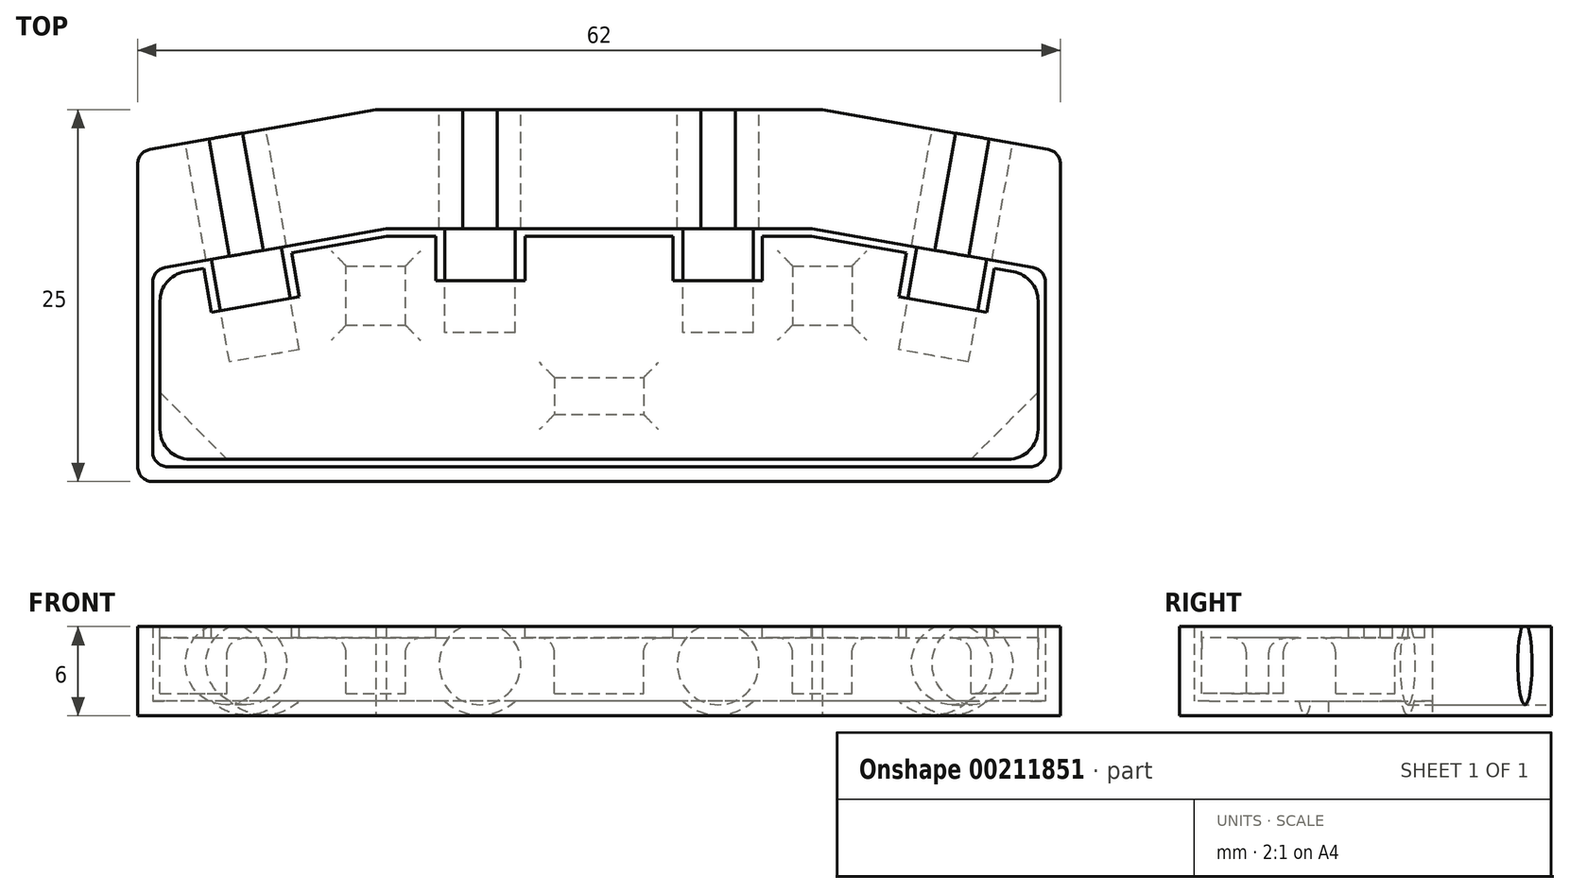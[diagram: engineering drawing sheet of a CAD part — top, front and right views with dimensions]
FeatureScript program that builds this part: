
annotation { "Feature Type Name" : "Feature", "Feature Type Description" : "" }
export const myFeature = defineFeature(function(context is Context, id is Id, definition is map)
    precondition{}
    {
        {
            var Q0;
            Q0=qCreatedBy(makeId("Top.planeOp"),FACE);
            var sketch = newSketch(context, id + "F0", { "sketchPlane" : qUnion([Q0])});
            skLineSegment(sketch, "E0.top", {"start": v(-31, -12.5) * mm, "end": v(31, -12.5) * mm});
            skLineSegment(sketch, "E0.left", {"start": v(-31, 12.5) * mm, "end": v(-31, -12.5) * mm});
            skLineSegment(sketch, "E0.right", {"start": v(31, 12.5) * mm, "end": v(31, -12.5) * mm});
            skLineSegment(sketch, "E1", {"start": v(0, 0) * mm, "end": v(31, 0) * mm, "construction": true});
            skLineSegment(sketch, "E2", {"start": v(0, 0) * mm, "end": v(-31, 0) * mm, "construction": true});
            skLineSegment(sketch, "E3", {"start": v(0, 0) * mm, "end": v(0, -12.5) * mm, "construction": true});
            skLineSegment(sketch, "E4", {"start": v(0, 0) * mm, "end": v(0, 12.5) * mm, "construction": true});
            skLineSegment(sketch, "E5", {"start": v(-15, 12.5) * mm, "end": v(-31, 9.68) * mm});
            skLineSegment(sketch, "E6", {"start": v(15, 12.5) * mm, "end": v(31, 9.68) * mm});
            skLineSegment(sketch, "E7", {"start": v(0, 12.5) * mm, "end": v(15, 12.5) * mm});
            skLineSegment(sketch, "E8", {"start": v(31, 12.5) * mm, "end": v(15, 12.5) * mm});
            skLineSegment(sketch, "E9", {"start": v(-31, 12.5) * mm, "end": v(-15, 12.5) * mm});
            skLineSegment(sketch, "E10", {"start": v(-15, 12.5) * mm, "end": v(0, 12.5) * mm});
            skLineSegment(sketch, "E11", {"start": v(-31, 1.56) * mm, "end": v(-14.3, 4.5) * mm});
            skLineSegment(sketch, "E12", {"start": v(14.3, 4.5) * mm, "end": v(31, 1.56) * mm});
            skLineSegment(sketch, "E13", {"start": v(-14.3, 4.5) * mm, "end": v(0, 4.5) * mm});
            skLineSegment(sketch, "E14", {"start": v(0, 4.5) * mm, "end": v(14.3, 4.5) * mm});
            skLineSegment(sketch, "E15", {"start": v(-30, 1.73) * mm, "end": v(-30, -11.5) * mm});
            skLineSegment(sketch, "E16", {"start": v(-30, -11.5) * mm, "end": v(30, -11.5) * mm});
            skLineSegment(sketch, "E17", {"start": v(30, -11.5) * mm, "end": v(30, 1.73) * mm});
            skLineSegment(sketch, "E18", {"start": v(31, -8.28) * mm, "end": v(30, -8.28) * mm, "construction": true});
            skLineSegment(sketch, "E19", {"start": v(27.47, -11.5) * mm, "end": v(27.47, -12.5) * mm, "construction": true});
            skLineSegment(sketch, "E20", {"start": v(-31, -9.5) * mm, "end": v(-30, -9.5) * mm, "construction": true});
            skSolve(sketch);
        }
        {
            var Q0;
            {var subQ3=sQuery(id+"F0.wireOp",EDGE,"E5");Q0=makeQuery(id+"F0.imprint","IMPRINT",FACE,{"disambiguationData":[TD([[makeQuery(id+"F0.imprint","IMPRINT",EDGE,{"derivedFrom":subQ3}),1.0]])]});}
            var Q1;
            {var subQ1=sQuery(id+"F0.wireOp",EDGE,"E0.top");Q1=makeQuery(id+"F0.imprint","IMPRINT",FACE,{"disambiguationData":[TD([[makeQuery(id+"F0.imprint","IMPRINT",EDGE,{"derivedFrom":subQ1}),1.0]])]});}
            var Q2;
            {var subQ1=sQuery(id+"F0.wireOp",EDGE,"E13");Q2=makeQuery(id+"F0.imprint","IMPRINT",FACE,{"disambiguationData":[TD([[makeQuery(id+"F0.imprint","IMPRINT",EDGE,{"derivedFrom":subQ1}),-1.0]])]});}
            extrude(context, id + "F1", {"entities" : qUnion([Q0, Q1, Q2]), "depth" : 1 * mm});
        }
        {
            var Q0;
            {var subQ8=sQuery(id+"F0.wireOp",EDGE,"E5");Q0=makeQuery(id+"F0.imprint","IMPRINT",FACE,{"disambiguationData":[TD([[makeQuery(id+"F0.imprint","IMPRINT",EDGE,{"derivedFrom":subQ8}),1.0]])]});}
            var Q1;
            {var subQ1=sQuery(id+"F0.wireOp",EDGE,"E0.top");Q1=makeQuery(id+"F0.imprint","IMPRINT",FACE,{"disambiguationData":[TD([[makeQuery(id+"F0.imprint","IMPRINT",EDGE,{"derivedFrom":subQ1}),1.0]])]});}
            extrude(context, id + "F2", {"entities" : qUnion([Q0, Q1]), "operationType" : NewBodyOperationType.ADD, "depth" : 6 * mm});
        }
        {
            var Q0;
            {var subQ0=sQuery(id+"F0.wireOp",EDGE,"E10");var subQ1=sQuery(id+"F0.wireOp",EDGE,"E7");Q0=makeQuery(id+"F2.boolean.opBoolean","MERGE",FACE,{"derivedFrom":[makeQuery(id+"F1.opExtrude","SWEPT_FACE",FACE,{"disambiguationData":[OSD([subQ1,sQuery(id+"F0.wireOp",EDGE,"E8"),sQuery(id+"F0.wireOp",EDGE,"E9"),subQ0])]}),makeQuery(id+"F2.opExtrude","SWEPT_FACE",FACE,{"disambiguationData":[OSD([subQ1,subQ0])]})]});}
            var sketch = newSketch(context, id + "F3", { "sketchPlane" : qUnion([Q0])});
            skCircle(sketch, "E21", {"center": v(-8, 3.5) * mm, "radius": 2.75 * mm});
            skCircle(sketch, "E22", {"center": v(8, 3.5) * mm, "radius": 2.75 * mm});
            skLineSegment(sketch, "E23", {"start": v(-8, 3.5) * mm, "end": v(0, 3.5) * mm, "construction": true});
            skLineSegment(sketch, "E24", {"start": v(0, 3.5) * mm, "end": v(8, 3.5) * mm, "construction": true});
            skLineSegment(sketch, "E25", {"start": v(0, 3.5) * mm, "end": v(0, 6) * mm, "construction": true});
            skLineSegment(sketch, "E26", {"start": v(0, 3.5) * mm, "end": v(0, 0) * mm, "construction": true});
            skCircle(sketch, "E27", {"center": v(-8, 3.5) * mm, "radius": 3.45 * mm});
            skCircle(sketch, "E28", {"center": v(8, 3.5) * mm, "radius": 3.45 * mm});
            skSolve(sketch);
        }
        {
            var Q0;
            {var subQ0=sQuery(id+"F3.wireOp",EDGE,"E21");var subQ1=makeQuery(id+"F2.opExtrude","CAP_EDGE",EDGE,{"disambiguationData":[OSD([sQuery(id+"F0.wireOp",EDGE,"E7"),sQuery(id+"F0.wireOp",EDGE,"E10")])],"isStart":false});var subQ2=makeQuery(id+"F3.imprint","INTERSECT",VERTEX,{"disambiguationData":[OD(0.0)],"derivedFrom":[subQ1,subQ0]});Q0=makeQuery(id+"F3.imprint","IMPRINT",FACE,{"disambiguationData":[TD([[makeQuery(id+"F3.imprint","IMPRINT",EDGE,{"disambiguationData":[TD([[subQ2,-1.0]])],"derivedFrom":subQ0}),1.0]])]});}
            var Q1;
            {var subQ0=sQuery(id+"F3.wireOp",EDGE,"E22");var subQ1=makeQuery(id+"F2.opExtrude","CAP_EDGE",EDGE,{"disambiguationData":[OSD([sQuery(id+"F0.wireOp",EDGE,"E7"),sQuery(id+"F0.wireOp",EDGE,"E10")])],"isStart":false});var subQ2=makeQuery(id+"F3.imprint","INTERSECT",VERTEX,{"disambiguationData":[OD(0.0)],"derivedFrom":[subQ1,subQ0]});Q1=makeQuery(id+"F3.imprint","IMPRINT",FACE,{"disambiguationData":[TD([[makeQuery(id+"F3.imprint","IMPRINT",EDGE,{"disambiguationData":[TD([[subQ2,1.0]])],"derivedFrom":subQ0}),1.0]])]});}
            var Q2;
            {var subQ0=sQuery(id+"F3.wireOp",EDGE,"E22");var subQ1=makeQuery(id+"F2.opExtrude","CAP_EDGE",EDGE,{"disambiguationData":[OSD([sQuery(id+"F0.wireOp",EDGE,"E7"),sQuery(id+"F0.wireOp",EDGE,"E10")])],"isStart":false});var subQ2=makeQuery(id+"F3.imprint","INTERSECT",VERTEX,{"disambiguationData":[OD(0.0)],"derivedFrom":[subQ1,subQ0]});Q2=makeQuery(id+"F3.imprint","IMPRINT",FACE,{"disambiguationData":[TD([[makeQuery(id+"F3.imprint","IMPRINT",EDGE,{"disambiguationData":[TD([[subQ2,-1.0]])],"derivedFrom":subQ0}),1.0]])]});}
            extrude(context, id + "F4", {"entities" : qUnion([Q0, Q1, Q2]), "operationType" : NewBodyOperationType.REMOVE, "oppositeDirection" : true, "depth" : 8 * mm});
        }
        {
            var Q0;
            Q0=makeQuery(id+"F2.opExtrude","SWEPT_FACE",FACE,{"disambiguationData":[OSD([sQuery(id+"F0.wireOp",EDGE,"E6")])]});
            var sketch = newSketch(context, id + "F5", { "sketchPlane" : qUnion([Q0])});
            skCircle(sketch, "E29", {"center": v(-22.85, 3.5) * mm, "radius": 2.75 * mm});
            skCircle(sketch, "E30", {"center": v(-22.85, 3.5) * mm, "radius": 3.45 * mm});
            skSolve(sketch);
        }
        {
            var Q0;
            {var subQ0=sQuery(id+"F5.wireOp",EDGE,"E29");var subQ1=makeQuery(id+"F2.opExtrude","CAP_EDGE",EDGE,{"disambiguationData":[OSD([sQuery(id+"F0.wireOp",EDGE,"E6")])],"isStart":false});var subQ2=makeQuery(id+"F5.imprint","INTERSECT",VERTEX,{"disambiguationData":[OD(0.0)],"derivedFrom":[subQ1,subQ0]});Q0=makeQuery(id+"F5.imprint","IMPRINT",FACE,{"disambiguationData":[TD([[makeQuery(id+"F5.imprint","IMPRINT",EDGE,{"disambiguationData":[TD([[subQ2,-1.0]])],"derivedFrom":subQ0}),1.0]])]});}
            var Q1;
            {var subQ0=sQuery(id+"F5.wireOp",EDGE,"E29");var subQ1=makeQuery(id+"F2.opExtrude","CAP_EDGE",EDGE,{"disambiguationData":[OSD([sQuery(id+"F0.wireOp",EDGE,"E6")])],"isStart":false});var subQ2=makeQuery(id+"F5.imprint","INTERSECT",VERTEX,{"disambiguationData":[OD(0.0)],"derivedFrom":[subQ1,subQ0]});Q1=makeQuery(id+"F5.imprint","IMPRINT",FACE,{"disambiguationData":[TD([[makeQuery(id+"F5.imprint","IMPRINT",EDGE,{"disambiguationData":[TD([[subQ2,1.0]])],"derivedFrom":subQ0}),1.0]])]});}
            extrude(context, id + "F6", {"entities" : qUnion([Q0, Q1]), "operationType" : NewBodyOperationType.REMOVE, "oppositeDirection" : true, "depth" : 8 * mm});
        }
        {
            var Q0;
            {var subQ0=sQuery(id+"F0.wireOp",EDGE,"E5");Q0=makeQuery(id+"F2.boolean.opBoolean","MERGE",FACE,{"derivedFrom":[makeQuery(id+"F1.opExtrude","SWEPT_FACE",FACE,{"disambiguationData":[OSD([subQ0])]}),makeQuery(id+"F2.opExtrude","SWEPT_FACE",FACE,{"disambiguationData":[OSD([subQ0])]})]});}
            var sketch = newSketch(context, id + "F7", { "sketchPlane" : qUnion([Q0])});
            skCircle(sketch, "E31", {"center": v(22.85, 3.5) * mm, "radius": 2.75 * mm});
            skCircle(sketch, "E32", {"center": v(22.85, 3.5) * mm, "radius": 3.45 * mm});
            skSolve(sketch);
        }
        {
            var Q0;
            {var subQ0=sQuery(id+"F7.wireOp",EDGE,"E31");var subQ1=makeQuery(id+"F2.opExtrude","CAP_EDGE",EDGE,{"disambiguationData":[OSD([sQuery(id+"F0.wireOp",EDGE,"E5")])],"isStart":false});var subQ2=makeQuery(id+"F7.imprint","INTERSECT",VERTEX,{"disambiguationData":[OD(0.0)],"derivedFrom":[subQ1,subQ0]});Q0=makeQuery(id+"F7.imprint","IMPRINT",FACE,{"disambiguationData":[TD([[makeQuery(id+"F7.imprint","IMPRINT",EDGE,{"disambiguationData":[TD([[subQ2,-1.0]])],"derivedFrom":subQ0}),1.0]])]});}
            extrude(context, id + "F8", {"entities" : qUnion([Q0]), "operationType" : NewBodyOperationType.REMOVE, "oppositeDirection" : true, "depth" : 8 * mm});
        }
        {
            var Q0;
            {var subQ0=sQuery(id+"F5.wireOp",EDGE,"E29");var subQ1=makeQuery(id+"F2.opExtrude","CAP_EDGE",EDGE,{"disambiguationData":[OSD([sQuery(id+"F0.wireOp",EDGE,"E6")])],"isStart":false});var subQ2=makeQuery(id+"F5.imprint","INTERSECT",VERTEX,{"disambiguationData":[OD(0.0)],"derivedFrom":[subQ1,subQ0]});Q0=makeQuery(id+"F5.imprint","IMPRINT",FACE,{"disambiguationData":[TD([[makeQuery(id+"F5.imprint","IMPRINT",EDGE,{"disambiguationData":[TD([[subQ2,-1.0]])],"derivedFrom":subQ0}),1.0]])]});}
            var Q1;
            {var subQ1=sQuery(id+"F0.wireOp",EDGE,"E6");var subQ2=makeQuery(id+"F2.opExtrude","CAP_EDGE",EDGE,{"disambiguationData":[OSD([subQ1])],"isStart":false});var subQ6=sQuery(id+"F5.wireOp",EDGE,"E29");var subQ7=makeQuery(id+"F5.imprint","INTERSECT",VERTEX,{"disambiguationData":[OD(0.0)],"derivedFrom":[subQ2,subQ6]});Q1=makeQuery(id+"F5.imprint","IMPRINT",FACE,{"disambiguationData":[TD([[makeQuery(id+"F5.imprint","IMPRINT",EDGE,{"disambiguationData":[TD([[subQ7,-1.0]])],"derivedFrom":subQ6}),-1.0]])]});}
            extrude(context, id + "F9", {"entities" : qUnion([Q0, Q1]), "depth" : -15 * mm, "hasSecondDirection" : true, "secondDirectionOppositeDirection" : false, "secondDirectionDepth" : -8 * mm});
        }
        {
            var Q0;
            {var subQ1=sQuery(id+"F0.wireOp",EDGE,"E10");var subQ2=sQuery(id+"F0.wireOp",EDGE,"E7");var subQ3=makeQuery(id+"F2.opExtrude","CAP_EDGE",EDGE,{"disambiguationData":[OSD([subQ2,subQ1])],"isStart":false});var subQ5=sQuery(id+"F3.wireOp",EDGE,"E21");var subQ6=makeQuery(id+"F3.imprint","INTERSECT",VERTEX,{"disambiguationData":[OD(0.0)],"derivedFrom":[subQ3,subQ5]});Q0=makeQuery(id+"F3.imprint","IMPRINT",FACE,{"disambiguationData":[TD([[makeQuery(id+"F3.imprint","IMPRINT",EDGE,{"disambiguationData":[TD([[subQ6,-1.0]])],"derivedFrom":subQ5}),-1.0]])]});}
            var Q1;
            {var subQ0=sQuery(id+"F3.wireOp",EDGE,"E21");var subQ1=makeQuery(id+"F2.opExtrude","CAP_EDGE",EDGE,{"disambiguationData":[OSD([sQuery(id+"F0.wireOp",EDGE,"E7"),sQuery(id+"F0.wireOp",EDGE,"E10")])],"isStart":false});var subQ2=makeQuery(id+"F3.imprint","INTERSECT",VERTEX,{"disambiguationData":[OD(0.0)],"derivedFrom":[subQ1,subQ0]});Q1=makeQuery(id+"F3.imprint","IMPRINT",FACE,{"disambiguationData":[TD([[makeQuery(id+"F3.imprint","IMPRINT",EDGE,{"disambiguationData":[TD([[subQ2,-1.0]])],"derivedFrom":subQ0}),1.0]])]});}
            var Q2;
            {var subQ1=sQuery(id+"F0.wireOp",EDGE,"E10");var subQ2=sQuery(id+"F0.wireOp",EDGE,"E7");var subQ3=makeQuery(id+"F2.opExtrude","CAP_EDGE",EDGE,{"disambiguationData":[OSD([subQ2,subQ1])],"isStart":false});var subQ5=sQuery(id+"F3.wireOp",EDGE,"E22");var subQ6=makeQuery(id+"F3.imprint","INTERSECT",VERTEX,{"disambiguationData":[OD(0.0)],"derivedFrom":[subQ3,subQ5]});Q2=makeQuery(id+"F3.imprint","IMPRINT",FACE,{"disambiguationData":[TD([[makeQuery(id+"F3.imprint","IMPRINT",EDGE,{"disambiguationData":[TD([[subQ6,-1.0]])],"derivedFrom":subQ5}),-1.0]])]});}
            var Q3;
            {var subQ0=sQuery(id+"F3.wireOp",EDGE,"E22");var subQ1=makeQuery(id+"F2.opExtrude","CAP_EDGE",EDGE,{"disambiguationData":[OSD([sQuery(id+"F0.wireOp",EDGE,"E7"),sQuery(id+"F0.wireOp",EDGE,"E10")])],"isStart":false});var subQ2=makeQuery(id+"F3.imprint","INTERSECT",VERTEX,{"disambiguationData":[OD(0.0)],"derivedFrom":[subQ1,subQ0]});Q3=makeQuery(id+"F3.imprint","IMPRINT",FACE,{"disambiguationData":[TD([[makeQuery(id+"F3.imprint","IMPRINT",EDGE,{"disambiguationData":[TD([[subQ2,-1.0]])],"derivedFrom":subQ0}),1.0]])]});}
            extrude(context, id + "F10", {"entities" : qUnion([Q0, Q1, Q2, Q3]), "oppositeDirection" : true, "depth" : 15 * mm, "hasSecondDirection" : true, "secondDirectionOppositeDirection" : true, "secondDirectionDepth" : 8 * mm});
        }
        {
            var Q0;
            {var subQ1=sQuery(id+"F0.wireOp",EDGE,"E5");var subQ2=makeQuery(id+"F2.opExtrude","CAP_EDGE",EDGE,{"disambiguationData":[OSD([subQ1])],"isStart":false});var subQ6=sQuery(id+"F7.wireOp",EDGE,"E31");var subQ7=makeQuery(id+"F7.imprint","INTERSECT",VERTEX,{"disambiguationData":[OD(0.0)],"derivedFrom":[subQ2,subQ6]});Q0=makeQuery(id+"F7.imprint","IMPRINT",FACE,{"disambiguationData":[TD([[makeQuery(id+"F7.imprint","IMPRINT",EDGE,{"disambiguationData":[TD([[subQ7,-1.0]])],"derivedFrom":subQ6}),-1.0]])]});}
            var Q1;
            {var subQ0=sQuery(id+"F7.wireOp",EDGE,"E31");var subQ1=makeQuery(id+"F2.opExtrude","CAP_EDGE",EDGE,{"disambiguationData":[OSD([sQuery(id+"F0.wireOp",EDGE,"E5")])],"isStart":false});var subQ2=makeQuery(id+"F7.imprint","INTERSECT",VERTEX,{"disambiguationData":[OD(0.0)],"derivedFrom":[subQ1,subQ0]});Q1=makeQuery(id+"F7.imprint","IMPRINT",FACE,{"disambiguationData":[TD([[makeQuery(id+"F7.imprint","IMPRINT",EDGE,{"disambiguationData":[TD([[subQ2,-1.0]])],"derivedFrom":subQ0}),1.0]])]});}
            extrude(context, id + "F11", {"entities" : qUnion([Q0, Q1]), "oppositeDirection" : true, "depth" : 15 * mm, "hasSecondDirection" : true, "secondDirectionOppositeDirection" : true, "secondDirectionDepth" : 8 * mm});
        }
        {
            var Q0;
            {var subQ0=sQuery(id+"F5.wireOp",EDGE,"E29");var subQ1=makeQuery(id+"F2.opExtrude","CAP_EDGE",EDGE,{"disambiguationData":[OSD([sQuery(id+"F0.wireOp",EDGE,"E6")])],"isStart":false});var subQ2=makeQuery(id+"F5.imprint","INTERSECT",VERTEX,{"disambiguationData":[OD(0.0)],"derivedFrom":[subQ1,subQ0]});Q0=makeQuery(id+"F5.imprint","IMPRINT",FACE,{"disambiguationData":[TD([[makeQuery(id+"F5.imprint","IMPRINT",EDGE,{"disambiguationData":[TD([[subQ2,1.0]])],"derivedFrom":subQ0}),-1.0]])]});}
            var Q1;
            {var subQ0=sQuery(id+"F5.wireOp",EDGE,"E29");var subQ1=makeQuery(id+"F2.opExtrude","CAP_EDGE",EDGE,{"disambiguationData":[OSD([sQuery(id+"F0.wireOp",EDGE,"E6")])],"isStart":false});var subQ2=makeQuery(id+"F5.imprint","INTERSECT",VERTEX,{"disambiguationData":[OD(0.0)],"derivedFrom":[subQ1,subQ0]});Q1=makeQuery(id+"F5.imprint","IMPRINT",FACE,{"disambiguationData":[TD([[makeQuery(id+"F5.imprint","IMPRINT",EDGE,{"disambiguationData":[TD([[subQ2,1.0]])],"derivedFrom":subQ0}),1.0]])]});}
            extrude(context, id + "F12", {"entities" : qUnion([Q0, Q1]), "operationType" : NewBodyOperationType.REMOVE, "oppositeDirection" : true, "depth" : 15 * mm, "hasSecondDirection" : true, "secondDirectionOppositeDirection" : true, "secondDirectionDepth" : 8 * mm});
        }
        {
            var Q0;
            Q0=makeQuery(id+"F11.opExtrude","SWEPT_BODY",BODY,{"disambiguationData":[OSD([sQuery(id+"F0.wireOp",EDGE,"E5"),sQuery(id+"F7.wireOp",EDGE,"E32")])]});
            var Q1;
            Q1=makeQuery(id+"F10.opExtrude","SWEPT_BODY",BODY,{"disambiguationData":[OSD([sQuery(id+"F0.wireOp",EDGE,"E7"),sQuery(id+"F0.wireOp",EDGE,"E10"),sQuery(id+"F3.wireOp",EDGE,"E28")])]});
            var Q2;
            Q2=makeQuery(id+"F10.opExtrude","SWEPT_BODY",BODY,{"disambiguationData":[OSD([sQuery(id+"F0.wireOp",EDGE,"E7"),sQuery(id+"F0.wireOp",EDGE,"E10"),sQuery(id+"F3.wireOp",EDGE,"E27")])]});
            var Q3;
            Q3=makeQuery(id+"F9.opExtrude","SWEPT_BODY",BODY,{"disambiguationData":[OSD([sQuery(id+"F0.wireOp",EDGE,"E6"),sQuery(id+"F5.wireOp",EDGE,"E30")])]});
            deleteBodies(context, id + "F13", {"entities" : qUnion([Q0, Q1, Q2, Q3])});
        }
        {
            var Q0;
            {var subQ0=sQuery(id+"F3.wireOp",EDGE,"E21");var subQ1=makeQuery(id+"F2.opExtrude","CAP_EDGE",EDGE,{"disambiguationData":[OSD([sQuery(id+"F0.wireOp",EDGE,"E7"),sQuery(id+"F0.wireOp",EDGE,"E10")])],"isStart":false});var subQ2=makeQuery(id+"F3.imprint","INTERSECT",VERTEX,{"disambiguationData":[OD(0.0)],"derivedFrom":[subQ1,subQ0]});Q0=makeQuery(id+"F3.imprint","IMPRINT",FACE,{"disambiguationData":[TD([[makeQuery(id+"F3.imprint","IMPRINT",EDGE,{"disambiguationData":[TD([[subQ2,-1.0]])],"derivedFrom":subQ0}),-1.0]])]});}
            var Q1;
            {var subQ0=sQuery(id+"F3.wireOp",EDGE,"E21");var subQ1=makeQuery(id+"F2.opExtrude","CAP_EDGE",EDGE,{"disambiguationData":[OSD([sQuery(id+"F0.wireOp",EDGE,"E7"),sQuery(id+"F0.wireOp",EDGE,"E10")])],"isStart":false});var subQ2=makeQuery(id+"F3.imprint","INTERSECT",VERTEX,{"disambiguationData":[OD(0.0)],"derivedFrom":[subQ1,subQ0]});Q1=makeQuery(id+"F3.imprint","IMPRINT",FACE,{"disambiguationData":[TD([[makeQuery(id+"F3.imprint","IMPRINT",EDGE,{"disambiguationData":[TD([[subQ2,-1.0]])],"derivedFrom":subQ0}),1.0]])]});}
            var Q2;
            {var subQ0=sQuery(id+"F3.wireOp",EDGE,"E22");var subQ1=makeQuery(id+"F2.opExtrude","CAP_EDGE",EDGE,{"disambiguationData":[OSD([sQuery(id+"F0.wireOp",EDGE,"E7"),sQuery(id+"F0.wireOp",EDGE,"E10")])],"isStart":false});var subQ2=makeQuery(id+"F3.imprint","INTERSECT",VERTEX,{"disambiguationData":[OD(0.0)],"derivedFrom":[subQ1,subQ0]});Q2=makeQuery(id+"F3.imprint","IMPRINT",FACE,{"disambiguationData":[TD([[makeQuery(id+"F3.imprint","IMPRINT",EDGE,{"disambiguationData":[TD([[subQ2,1.0]])],"derivedFrom":subQ0}),-1.0]])]});}
            var Q3;
            {var subQ0=sQuery(id+"F3.wireOp",EDGE,"E22");var subQ1=makeQuery(id+"F2.opExtrude","CAP_EDGE",EDGE,{"disambiguationData":[OSD([sQuery(id+"F0.wireOp",EDGE,"E7"),sQuery(id+"F0.wireOp",EDGE,"E10")])],"isStart":false});var subQ2=makeQuery(id+"F3.imprint","INTERSECT",VERTEX,{"disambiguationData":[OD(0.0)],"derivedFrom":[subQ1,subQ0]});Q3=makeQuery(id+"F3.imprint","IMPRINT",FACE,{"disambiguationData":[TD([[makeQuery(id+"F3.imprint","IMPRINT",EDGE,{"disambiguationData":[TD([[subQ2,1.0]])],"derivedFrom":subQ0}),1.0]])]});}
            extrude(context, id + "F14", {"entities" : qUnion([Q0, Q1, Q2, Q3]), "operationType" : NewBodyOperationType.REMOVE, "oppositeDirection" : true, "depth" : 15 * mm, "hasSecondDirection" : true, "secondDirectionOppositeDirection" : true, "secondDirectionDepth" : 8 * mm});
        }
        {
            var Q0;
            {var subQ0=sQuery(id+"F7.wireOp",EDGE,"E31");var subQ1=makeQuery(id+"F2.opExtrude","CAP_EDGE",EDGE,{"disambiguationData":[OSD([sQuery(id+"F0.wireOp",EDGE,"E5")])],"isStart":false});var subQ2=makeQuery(id+"F7.imprint","INTERSECT",VERTEX,{"disambiguationData":[OD(0.0)],"derivedFrom":[subQ1,subQ0]});Q0=makeQuery(id+"F7.imprint","IMPRINT",FACE,{"disambiguationData":[TD([[makeQuery(id+"F7.imprint","IMPRINT",EDGE,{"disambiguationData":[TD([[subQ2,-1.0]])],"derivedFrom":subQ0}),-1.0]])]});}
            var Q1;
            {var subQ0=sQuery(id+"F7.wireOp",EDGE,"E31");var subQ1=makeQuery(id+"F2.opExtrude","CAP_EDGE",EDGE,{"disambiguationData":[OSD([sQuery(id+"F0.wireOp",EDGE,"E5")])],"isStart":false});var subQ2=makeQuery(id+"F7.imprint","INTERSECT",VERTEX,{"disambiguationData":[OD(0.0)],"derivedFrom":[subQ1,subQ0]});Q1=makeQuery(id+"F7.imprint","IMPRINT",FACE,{"disambiguationData":[TD([[makeQuery(id+"F7.imprint","IMPRINT",EDGE,{"disambiguationData":[TD([[subQ2,-1.0]])],"derivedFrom":subQ0}),1.0]])]});}
            extrude(context, id + "F15", {"entities" : qUnion([Q0, Q1]), "operationType" : NewBodyOperationType.REMOVE, "oppositeDirection" : true, "depth" : 15 * mm, "hasSecondDirection" : true, "secondDirectionOppositeDirection" : true, "secondDirectionDepth" : 8 * mm});
        }
        {
            var Q0;
            {var subQ0=sQuery(id+"F0.wireOp",EDGE,"E6");var subQ1=sQuery(id+"F0.wireOp",EDGE,"E0.right");Q0=makeQuery(id+"F2.boolean.opBoolean","MERGE",EDGE,{"derivedFrom":[makeQuery(id+"F1.opExtrude","SWEPT_EDGE",EDGE,{"disambiguationData":[OSD([subQ1,subQ0])]}),makeQuery(id+"F2.opExtrude","SWEPT_EDGE",EDGE,{"disambiguationData":[OSD([subQ1,subQ0])]})]});}
            var Q1;
            {var subQ0=sQuery(id+"F0.wireOp",EDGE,"E5");var subQ1=sQuery(id+"F0.wireOp",EDGE,"E0.left");Q1=makeQuery(id+"F2.boolean.opBoolean","MERGE",EDGE,{"derivedFrom":[makeQuery(id+"F1.opExtrude","SWEPT_EDGE",EDGE,{"disambiguationData":[OSD([subQ1,subQ0])]}),makeQuery(id+"F2.opExtrude","SWEPT_EDGE",EDGE,{"disambiguationData":[OSD([subQ1,subQ0])]})]});}
            var Q2;
            {var subQ0=sQuery(id+"F0.wireOp",EDGE,"E0.left");var subQ1=sQuery(id+"F0.wireOp",EDGE,"E0.top");Q2=makeQuery(id+"F2.boolean.opBoolean","MERGE",EDGE,{"derivedFrom":[makeQuery(id+"F1.opExtrude","SWEPT_EDGE",EDGE,{"disambiguationData":[OSD([subQ1,subQ0])]}),makeQuery(id+"F2.opExtrude","SWEPT_EDGE",EDGE,{"disambiguationData":[OSD([subQ1,subQ0])]})]});}
            var Q3;
            Q3=makeQuery(id+"F2.opExtrude","SWEPT_EDGE",EDGE,{"disambiguationData":[OSD([sQuery(id+"F0.wireOp",EDGE,"E15"),sQuery(id+"F0.wireOp",EDGE,"E16")])]});
            var Q4;
            Q4=makeQuery(id+"F2.opExtrude","SWEPT_EDGE",EDGE,{"disambiguationData":[OSD([sQuery(id+"F0.wireOp",EDGE,"E16"),sQuery(id+"F0.wireOp",EDGE,"E17")])]});
            var Q5;
            {var subQ0=sQuery(id+"F0.wireOp",EDGE,"E0.right");var subQ1=sQuery(id+"F0.wireOp",EDGE,"E0.top");Q5=makeQuery(id+"F2.boolean.opBoolean","MERGE",EDGE,{"derivedFrom":[makeQuery(id+"F1.opExtrude","SWEPT_EDGE",EDGE,{"disambiguationData":[OSD([subQ1,subQ0])]}),makeQuery(id+"F2.opExtrude","SWEPT_EDGE",EDGE,{"disambiguationData":[OSD([subQ1,subQ0])]})]});}
            var Q6;
            Q6=makeQuery(id+"F2.opExtrude","SWEPT_EDGE",EDGE,{"disambiguationData":[OSD([sQuery(id+"F0.wireOp",EDGE,"E12"),sQuery(id+"F0.wireOp",EDGE,"E17")])]});
            var Q7;
            Q7=makeQuery(id+"F2.opExtrude","SWEPT_EDGE",EDGE,{"disambiguationData":[OSD([sQuery(id+"F0.wireOp",EDGE,"E11"),sQuery(id+"F0.wireOp",EDGE,"E15")])]});
            fillet(context, id + "F16", {"entities" : qUnion([Q0, Q1, Q2, Q3, Q4, Q5, Q6, Q7]), "radius" : 1 * mm, "tangentPropagation" : true, "allowEdgeOverflow" : false});
        }
        {
            var Q0;
            {var subQ0=sQuery(id+"F0.wireOp",EDGE,"E14");var subQ1=sQuery(id+"F0.wireOp",EDGE,"E13");var subQ2=sQuery(id+"F0.wireOp",EDGE,"E10");var subQ3=sQuery(id+"F0.wireOp",EDGE,"E7");Q0=makeQuery(id+"F4.boolean.opBoolean","SPLIT",FACE,{"disambiguationData":[TD([makeQuery(id+"F1.opExtrude","SWEPT_FACE",FACE,{"disambiguationData":[OSD([subQ3,subQ2])]}),makeQuery(id+"F2.opExtrude","SWEPT_FACE",FACE,{"disambiguationData":[OSD([subQ3,subQ2])]}),makeQuery(id+"F2.opExtrude","SWEPT_FACE",FACE,{"disambiguationData":[OSD([subQ1,subQ0])]}),makeQuery(id+"F4.opExtrude","SWEPT_FACE",FACE,{"disambiguationData":[OSD([sQuery(id+"F3.wireOp",EDGE,"E21")])]}),makeQuery(id+"F4.opExtrude","SWEPT_FACE",FACE,{"disambiguationData":[OSD([sQuery(id+"F3.wireOp",EDGE,"E22")])]})])],"derivedFrom":makeQuery(id+"F2.opExtrude","CAP_FACE",FACE,{"disambiguationData":[OSD([sQuery(id+"F0.wireOp",EDGE,"E0.top"),sQuery(id+"F0.wireOp",EDGE,"E0.left"),sQuery(id+"F0.wireOp",EDGE,"E0.right"),sQuery(id+"F0.wireOp",EDGE,"E5"),sQuery(id+"F0.wireOp",EDGE,"E6"),subQ3,subQ2,sQuery(id+"F0.wireOp",EDGE,"E11"),sQuery(id+"F0.wireOp",EDGE,"E12"),subQ1,subQ0,sQuery(id+"F0.wireOp",EDGE,"E15"),sQuery(id+"F0.wireOp",EDGE,"E16"),sQuery(id+"F0.wireOp",EDGE,"E17")])],"isStart":false})});}
            cPlane(context, id + "F17", {"entities" : qUnion([Q0]), "cplaneType" : CPlaneType.OFFSET, "offset" : 0 * mm, "width" : 150 * mm, "height" : 150 * mm});
        }
        {
            var Q0;
            Q0=qCreatedBy(id+"F17.planeOp",FACE);
            var sketch = newSketch(context, id + "F18", { "sketchPlane" : qUnion([Q0])});
            skLineSegment(sketch, "E33", {"start": v(-27.5, -11) * mm, "end": v(27.5, -11) * mm});
            skLineSegment(sketch, "E34", {"start": v(29.5, -9) * mm, "end": v(29.5, -0.37) * mm});
            skLineSegment(sketch, "E35", {"start": v(27.85, 1.6) * mm, "end": v(26.57, 1.83) * mm});
            skLineSegment(sketch, "E36", {"start": v(14.26, 4) * mm, "end": v(10.98, 4) * mm});
            skLineSegment(sketch, "E37", {"start": v(-14.26, 4) * mm, "end": v(-20.66, 2.87) * mm});
            skLineSegment(sketch, "E38", {"start": v(-29.5, -0.37) * mm, "end": v(-29.5, -9) * mm});
            skLineSegment(sketch, "E39.bottom", {"start": v(-17, -2) * mm, "end": v(-13, -2) * mm});
            skLineSegment(sketch, "E39.top", {"start": v(-17, 2) * mm, "end": v(-13, 2) * mm});
            skLineSegment(sketch, "E39.left", {"start": v(-17, -2) * mm, "end": v(-17, 2) * mm});
            skLineSegment(sketch, "E39.right", {"start": v(-13, -2) * mm, "end": v(-13, 2) * mm});
            skLineSegment(sketch, "E40.bottom", {"start": v(13, 2) * mm, "end": v(17, 2) * mm});
            skLineSegment(sketch, "E40.top", {"start": v(13, -2) * mm, "end": v(17, -2) * mm});
            skLineSegment(sketch, "E40.left", {"start": v(13, 2) * mm, "end": v(13, -2) * mm});
            skLineSegment(sketch, "E40.right", {"start": v(17, 2) * mm, "end": v(17, -2) * mm});
            skLineSegment(sketch, "E41", {"start": v(17, 0) * mm, "end": v(13, 0) * mm, "construction": true});
            skLineSegment(sketch, "E42", {"start": v(13, 0) * mm, "end": v(0, 0) * mm, "construction": true});
            skLineSegment(sketch, "E43", {"start": v(-17, 0) * mm, "end": v(-13, 0) * mm, "construction": true});
            skLineSegment(sketch, "E44", {"start": v(-13, 0) * mm, "end": v(0, 0) * mm, "construction": true});
            skPoint(sketch, "E45.visualSharp", {"position": v(-29.5, 1.31) * mm});
            skArc(sketch, "E45.filletArc", {"start": v(-27.85, 1.6) * mm, "mid": v(-29.03, 0.92) * mm, "end": v(-29.5, -0.37) * mm});
            skPoint(sketch, "E46.visualSharp", {"position": v(-29.5, -11) * mm});
            skArc(sketch, "E46.filletArc", {"start": v(-29.5, -9) * mm, "mid": v(-28.91, -10.41) * mm, "end": v(-27.5, -11) * mm});
            skPoint(sketch, "E47.visualSharp", {"position": v(29.5, -11) * mm});
            skArc(sketch, "E47.filletArc", {"start": v(27.5, -11) * mm, "mid": v(28.91, -10.41) * mm, "end": v(29.5, -9) * mm});
            skPoint(sketch, "E48.visualSharp", {"position": v(29.5, 1.31) * mm});
            skArc(sketch, "E48.filletArc", {"start": v(29.5, -0.37) * mm, "mid": v(29.03, 0.92) * mm, "end": v(27.85, 1.6) * mm});
            skLineSegment(sketch, "E49.bottom", {"start": v(-3, -5.5) * mm, "end": v(3, -5.5) * mm});
            skLineSegment(sketch, "E49.top", {"start": v(-3, -8) * mm, "end": v(3, -8) * mm});
            skLineSegment(sketch, "E49.left", {"start": v(-3, -5.5) * mm, "end": v(-3, -8) * mm});
            skLineSegment(sketch, "E49.right", {"start": v(3, -5.5) * mm, "end": v(3, -8) * mm});
            skLineSegment(sketch, "E50", {"start": v(0, -5.5) * mm, "end": v(0, 0) * mm, "construction": true});
            skLineSegment(sketch, "E51", {"start": v(-29.5, -6.5) * mm, "end": v(-25, -11) * mm});
            skLineSegment(sketch, "E52", {"start": v(29.5, -6.5) * mm, "end": v(25, -11) * mm});
            skLineSegment(sketch, "E53", {"start": v(-26.57, 1.83) * mm, "end": v(-26.05, -1.13) * mm});
            skLineSegment(sketch, "E54", {"start": v(-26.05, -1.13) * mm, "end": v(-20.14, -0.08) * mm});
            skLineSegment(sketch, "E55", {"start": v(-20.14, -0.08) * mm, "end": v(-20.66, 2.87) * mm});
            skLineSegment(sketch, "E56", {"start": v(-10.98, 4) * mm, "end": v(-10.98, 1) * mm});
            skLineSegment(sketch, "E57", {"start": v(-10.98, 1) * mm, "end": v(-4.98, 1) * mm});
            skLineSegment(sketch, "E58", {"start": v(-4.98, 1) * mm, "end": v(-4.98, 4) * mm});
            skLineSegment(sketch, "E59", {"start": v(4.98, 4) * mm, "end": v(4.98, 1) * mm});
            skLineSegment(sketch, "E60", {"start": v(4.98, 1) * mm, "end": v(10.98, 1) * mm});
            skLineSegment(sketch, "E61", {"start": v(10.98, 1) * mm, "end": v(10.98, 4) * mm});
            skLineSegment(sketch, "E62", {"start": v(20.66, 2.87) * mm, "end": v(20.14, -0.08) * mm});
            skLineSegment(sketch, "E63", {"start": v(20.14, -0.08) * mm, "end": v(26.05, -1.13) * mm});
            skLineSegment(sketch, "E64", {"start": v(26.05, -1.13) * mm, "end": v(26.57, 1.83) * mm});
            skLineSegment(sketch, "E65.trimOffspring", {"start": v(-26.57, 1.83) * mm, "end": v(-27.85, 1.6) * mm});
            skLineSegment(sketch, "E66.trimOffspring", {"start": v(-10.98, 4) * mm, "end": v(-14.26, 4) * mm});
            skLineSegment(sketch, "E67.trimOffspring", {"start": v(4.98, 4) * mm, "end": v(-4.98, 4) * mm});
            skLineSegment(sketch, "E68.trimOffspring", {"start": v(20.66, 2.87) * mm, "end": v(14.26, 4) * mm});
            skSolve(sketch);
        }
        {
            var Q0;
            Q0 = qSketchRegion(id + "F18", true);
            var Q1;
            Q1=makeQuery(id+"F18.imprint","IMPRINT",FACE,{"disambiguationData":[TD([[makeQuery(id+"F18.imprint","IMPRINT",EDGE,{"derivedFrom":sQuery(id+"F18.wireOp",EDGE,"E39.bottom")}),1.0]])]});
            var Q2;
            Q2=makeQuery(id+"F18.imprint","IMPRINT",FACE,{"disambiguationData":[TD([[makeQuery(id+"F18.imprint","IMPRINT",EDGE,{"derivedFrom":sQuery(id+"F18.wireOp",EDGE,"E49.bottom")}),-1.0]])]});
            var Q3;
            Q3=makeQuery(id+"F18.imprint","IMPRINT",FACE,{"disambiguationData":[TD([[makeQuery(id+"F18.imprint","IMPRINT",EDGE,{"derivedFrom":sQuery(id+"F18.wireOp",EDGE,"E40.bottom")}),-1.0]])]});
            extrude(context, id + "F19", {"entities" : qUnion([Q0, Q1, Q2, Q3]), "oppositeDirection" : true, "depth" : 0.75 * mm, "offsetDistance" : 25 * mm});
        }
        {
            var Q0;
            Q0=makeQuery(id+"F18.imprint","IMPRINT",FACE,{"disambiguationData":[TD([[makeQuery(id+"F18.imprint","IMPRINT",EDGE,{"derivedFrom":sQuery(id+"F18.wireOp",EDGE,"E49.bottom")}),-1.0]])]});
            var Q1;
            Q1=makeQuery(id+"F18.imprint","IMPRINT",FACE,{"disambiguationData":[TD([[makeQuery(id+"F18.imprint","IMPRINT",EDGE,{"derivedFrom":sQuery(id+"F18.wireOp",EDGE,"E39.bottom")}),1.0]])]});
            var Q2;
            {var subQ2=sQuery(id+"F18.wireOp",EDGE,"E46.filletArc");Q2=makeQuery(id+"F18.imprint","IMPRINT",FACE,{"disambiguationData":[TD([[makeQuery(id+"F18.imprint","IMPRINT",EDGE,{"derivedFrom":subQ2}),1.0]])]});}
            var Q3;
            Q3=makeQuery(id+"F18.imprint","IMPRINT",FACE,{"disambiguationData":[TD([[makeQuery(id+"F18.imprint","IMPRINT",EDGE,{"derivedFrom":sQuery(id+"F18.wireOp",EDGE,"E40.bottom")}),-1.0]])]});
            var Q4;
            {var subQ0=sQuery(id+"F18.wireOp",EDGE,"E47.filletArc");Q4=makeQuery(id+"F18.imprint","IMPRINT",FACE,{"disambiguationData":[TD([[makeQuery(id+"F18.imprint","IMPRINT",EDGE,{"derivedFrom":subQ0}),1.0]])]});}
            extrude(context, id + "F20", {"entities" : qUnion([Q0, Q1, Q2, Q3, Q4]), "operationType" : NewBodyOperationType.ADD, "oppositeDirection" : true, "depth" : 4.5 * mm, "offsetDistance" : 25 * mm});
        }
        {
            var Q0;
            Q0=makeQuery(id+"F20.boolean.opBoolean","INTERSECT",EDGE,{"derivedFrom":[makeQuery(id+"F19.opExtrude","CAP_FACE",FACE,{"disambiguationData":[OSD([sQuery(id+"F18.wireOp",EDGE,"E33"),sQuery(id+"F18.wireOp",EDGE,"E34"),sQuery(id+"F18.wireOp",EDGE,"E35"),sQuery(id+"F18.wireOp",EDGE,"E36"),sQuery(id+"F18.wireOp",EDGE,"E37"),sQuery(id+"F18.wireOp",EDGE,"E38"),sQuery(id+"F18.wireOp",EDGE,"E45.filletArc"),sQuery(id+"F18.wireOp",EDGE,"E46.filletArc"),sQuery(id+"F18.wireOp",EDGE,"E47.filletArc"),sQuery(id+"F18.wireOp",EDGE,"E48.filletArc"),sQuery(id+"F18.wireOp",EDGE,"E53"),sQuery(id+"F18.wireOp",EDGE,"E54"),sQuery(id+"F18.wireOp",EDGE,"E55"),sQuery(id+"F18.wireOp",EDGE,"E56"),sQuery(id+"F18.wireOp",EDGE,"E57"),sQuery(id+"F18.wireOp",EDGE,"E58"),sQuery(id+"F18.wireOp",EDGE,"E59"),sQuery(id+"F18.wireOp",EDGE,"E60"),sQuery(id+"F18.wireOp",EDGE,"E61"),sQuery(id+"F18.wireOp",EDGE,"E62"),sQuery(id+"F18.wireOp",EDGE,"E63"),sQuery(id+"F18.wireOp",EDGE,"E64"),sQuery(id+"F18.wireOp",EDGE,"E65.trimOffspring"),sQuery(id+"F18.wireOp",EDGE,"E66.trimOffspring"),sQuery(id+"F18.wireOp",EDGE,"E67.trimOffspring"),sQuery(id+"F18.wireOp",EDGE,"E68.trimOffspring")])],"isStart":false}),makeQuery(id+"F20.opExtrude","SWEPT_FACE",FACE,{"disambiguationData":[OSD([sQuery(id+"F18.wireOp",EDGE,"E49.top")])]})]});
            var Q1;
            Q1=makeQuery(id+"F20.boolean.opBoolean","INTERSECT",EDGE,{"derivedFrom":[makeQuery(id+"F19.opExtrude","CAP_FACE",FACE,{"disambiguationData":[OSD([sQuery(id+"F18.wireOp",EDGE,"E33"),sQuery(id+"F18.wireOp",EDGE,"E34"),sQuery(id+"F18.wireOp",EDGE,"E35"),sQuery(id+"F18.wireOp",EDGE,"E36"),sQuery(id+"F18.wireOp",EDGE,"E37"),sQuery(id+"F18.wireOp",EDGE,"E38"),sQuery(id+"F18.wireOp",EDGE,"E45.filletArc"),sQuery(id+"F18.wireOp",EDGE,"E46.filletArc"),sQuery(id+"F18.wireOp",EDGE,"E47.filletArc"),sQuery(id+"F18.wireOp",EDGE,"E48.filletArc"),sQuery(id+"F18.wireOp",EDGE,"E53"),sQuery(id+"F18.wireOp",EDGE,"E54"),sQuery(id+"F18.wireOp",EDGE,"E55"),sQuery(id+"F18.wireOp",EDGE,"E56"),sQuery(id+"F18.wireOp",EDGE,"E57"),sQuery(id+"F18.wireOp",EDGE,"E58"),sQuery(id+"F18.wireOp",EDGE,"E59"),sQuery(id+"F18.wireOp",EDGE,"E60"),sQuery(id+"F18.wireOp",EDGE,"E61"),sQuery(id+"F18.wireOp",EDGE,"E62"),sQuery(id+"F18.wireOp",EDGE,"E63"),sQuery(id+"F18.wireOp",EDGE,"E64"),sQuery(id+"F18.wireOp",EDGE,"E65.trimOffspring"),sQuery(id+"F18.wireOp",EDGE,"E66.trimOffspring"),sQuery(id+"F18.wireOp",EDGE,"E67.trimOffspring"),sQuery(id+"F18.wireOp",EDGE,"E68.trimOffspring")])],"isStart":false}),makeQuery(id+"F20.opExtrude","SWEPT_FACE",FACE,{"disambiguationData":[OSD([sQuery(id+"F18.wireOp",EDGE,"E49.right")])]})]});
            var Q2;
            Q2=makeQuery(id+"F20.boolean.opBoolean","INTERSECT",EDGE,{"derivedFrom":[makeQuery(id+"F19.opExtrude","CAP_FACE",FACE,{"disambiguationData":[OSD([sQuery(id+"F18.wireOp",EDGE,"E33"),sQuery(id+"F18.wireOp",EDGE,"E34"),sQuery(id+"F18.wireOp",EDGE,"E35"),sQuery(id+"F18.wireOp",EDGE,"E36"),sQuery(id+"F18.wireOp",EDGE,"E37"),sQuery(id+"F18.wireOp",EDGE,"E38"),sQuery(id+"F18.wireOp",EDGE,"E45.filletArc"),sQuery(id+"F18.wireOp",EDGE,"E46.filletArc"),sQuery(id+"F18.wireOp",EDGE,"E47.filletArc"),sQuery(id+"F18.wireOp",EDGE,"E48.filletArc"),sQuery(id+"F18.wireOp",EDGE,"E53"),sQuery(id+"F18.wireOp",EDGE,"E54"),sQuery(id+"F18.wireOp",EDGE,"E55"),sQuery(id+"F18.wireOp",EDGE,"E56"),sQuery(id+"F18.wireOp",EDGE,"E57"),sQuery(id+"F18.wireOp",EDGE,"E58"),sQuery(id+"F18.wireOp",EDGE,"E59"),sQuery(id+"F18.wireOp",EDGE,"E60"),sQuery(id+"F18.wireOp",EDGE,"E61"),sQuery(id+"F18.wireOp",EDGE,"E62"),sQuery(id+"F18.wireOp",EDGE,"E63"),sQuery(id+"F18.wireOp",EDGE,"E64"),sQuery(id+"F18.wireOp",EDGE,"E65.trimOffspring"),sQuery(id+"F18.wireOp",EDGE,"E66.trimOffspring"),sQuery(id+"F18.wireOp",EDGE,"E67.trimOffspring"),sQuery(id+"F18.wireOp",EDGE,"E68.trimOffspring")])],"isStart":false}),makeQuery(id+"F20.opExtrude","SWEPT_FACE",FACE,{"disambiguationData":[OSD([sQuery(id+"F18.wireOp",EDGE,"E49.left")])]})]});
            var Q3;
            Q3=makeQuery(id+"F20.boolean.opBoolean","INTERSECT",EDGE,{"derivedFrom":[makeQuery(id+"F19.opExtrude","CAP_FACE",FACE,{"disambiguationData":[OSD([sQuery(id+"F18.wireOp",EDGE,"E33"),sQuery(id+"F18.wireOp",EDGE,"E34"),sQuery(id+"F18.wireOp",EDGE,"E35"),sQuery(id+"F18.wireOp",EDGE,"E36"),sQuery(id+"F18.wireOp",EDGE,"E37"),sQuery(id+"F18.wireOp",EDGE,"E38"),sQuery(id+"F18.wireOp",EDGE,"E45.filletArc"),sQuery(id+"F18.wireOp",EDGE,"E46.filletArc"),sQuery(id+"F18.wireOp",EDGE,"E47.filletArc"),sQuery(id+"F18.wireOp",EDGE,"E48.filletArc"),sQuery(id+"F18.wireOp",EDGE,"E53"),sQuery(id+"F18.wireOp",EDGE,"E54"),sQuery(id+"F18.wireOp",EDGE,"E55"),sQuery(id+"F18.wireOp",EDGE,"E56"),sQuery(id+"F18.wireOp",EDGE,"E57"),sQuery(id+"F18.wireOp",EDGE,"E58"),sQuery(id+"F18.wireOp",EDGE,"E59"),sQuery(id+"F18.wireOp",EDGE,"E60"),sQuery(id+"F18.wireOp",EDGE,"E61"),sQuery(id+"F18.wireOp",EDGE,"E62"),sQuery(id+"F18.wireOp",EDGE,"E63"),sQuery(id+"F18.wireOp",EDGE,"E64"),sQuery(id+"F18.wireOp",EDGE,"E65.trimOffspring"),sQuery(id+"F18.wireOp",EDGE,"E66.trimOffspring"),sQuery(id+"F18.wireOp",EDGE,"E67.trimOffspring"),sQuery(id+"F18.wireOp",EDGE,"E68.trimOffspring")])],"isStart":false}),makeQuery(id+"F20.opExtrude","SWEPT_FACE",FACE,{"disambiguationData":[OSD([sQuery(id+"F18.wireOp",EDGE,"E49.bottom")])]})]});
            var Q4;
            Q4=makeQuery(id+"F20.boolean.opBoolean","INTERSECT",EDGE,{"derivedFrom":[makeQuery(id+"F19.opExtrude","CAP_FACE",FACE,{"disambiguationData":[OSD([sQuery(id+"F18.wireOp",EDGE,"E33"),sQuery(id+"F18.wireOp",EDGE,"E34"),sQuery(id+"F18.wireOp",EDGE,"E35"),sQuery(id+"F18.wireOp",EDGE,"E36"),sQuery(id+"F18.wireOp",EDGE,"E37"),sQuery(id+"F18.wireOp",EDGE,"E38"),sQuery(id+"F18.wireOp",EDGE,"E45.filletArc"),sQuery(id+"F18.wireOp",EDGE,"E46.filletArc"),sQuery(id+"F18.wireOp",EDGE,"E47.filletArc"),sQuery(id+"F18.wireOp",EDGE,"E48.filletArc"),sQuery(id+"F18.wireOp",EDGE,"E53"),sQuery(id+"F18.wireOp",EDGE,"E54"),sQuery(id+"F18.wireOp",EDGE,"E55"),sQuery(id+"F18.wireOp",EDGE,"E56"),sQuery(id+"F18.wireOp",EDGE,"E57"),sQuery(id+"F18.wireOp",EDGE,"E58"),sQuery(id+"F18.wireOp",EDGE,"E59"),sQuery(id+"F18.wireOp",EDGE,"E60"),sQuery(id+"F18.wireOp",EDGE,"E61"),sQuery(id+"F18.wireOp",EDGE,"E62"),sQuery(id+"F18.wireOp",EDGE,"E63"),sQuery(id+"F18.wireOp",EDGE,"E64"),sQuery(id+"F18.wireOp",EDGE,"E65.trimOffspring"),sQuery(id+"F18.wireOp",EDGE,"E66.trimOffspring"),sQuery(id+"F18.wireOp",EDGE,"E67.trimOffspring"),sQuery(id+"F18.wireOp",EDGE,"E68.trimOffspring")])],"isStart":false}),makeQuery(id+"F20.opExtrude","SWEPT_FACE",FACE,{"disambiguationData":[OSD([sQuery(id+"F18.wireOp",EDGE,"E39.bottom")])]})]});
            var Q5;
            Q5=makeQuery(id+"F20.boolean.opBoolean","INTERSECT",EDGE,{"derivedFrom":[makeQuery(id+"F19.opExtrude","CAP_FACE",FACE,{"disambiguationData":[OSD([sQuery(id+"F18.wireOp",EDGE,"E33"),sQuery(id+"F18.wireOp",EDGE,"E34"),sQuery(id+"F18.wireOp",EDGE,"E35"),sQuery(id+"F18.wireOp",EDGE,"E36"),sQuery(id+"F18.wireOp",EDGE,"E37"),sQuery(id+"F18.wireOp",EDGE,"E38"),sQuery(id+"F18.wireOp",EDGE,"E45.filletArc"),sQuery(id+"F18.wireOp",EDGE,"E46.filletArc"),sQuery(id+"F18.wireOp",EDGE,"E47.filletArc"),sQuery(id+"F18.wireOp",EDGE,"E48.filletArc"),sQuery(id+"F18.wireOp",EDGE,"E53"),sQuery(id+"F18.wireOp",EDGE,"E54"),sQuery(id+"F18.wireOp",EDGE,"E55"),sQuery(id+"F18.wireOp",EDGE,"E56"),sQuery(id+"F18.wireOp",EDGE,"E57"),sQuery(id+"F18.wireOp",EDGE,"E58"),sQuery(id+"F18.wireOp",EDGE,"E59"),sQuery(id+"F18.wireOp",EDGE,"E60"),sQuery(id+"F18.wireOp",EDGE,"E61"),sQuery(id+"F18.wireOp",EDGE,"E62"),sQuery(id+"F18.wireOp",EDGE,"E63"),sQuery(id+"F18.wireOp",EDGE,"E64"),sQuery(id+"F18.wireOp",EDGE,"E65.trimOffspring"),sQuery(id+"F18.wireOp",EDGE,"E66.trimOffspring"),sQuery(id+"F18.wireOp",EDGE,"E67.trimOffspring"),sQuery(id+"F18.wireOp",EDGE,"E68.trimOffspring")])],"isStart":false}),makeQuery(id+"F20.opExtrude","SWEPT_FACE",FACE,{"disambiguationData":[OSD([sQuery(id+"F18.wireOp",EDGE,"E39.left")])]})]});
            var Q6;
            Q6=makeQuery(id+"F20.boolean.opBoolean","INTERSECT",EDGE,{"derivedFrom":[makeQuery(id+"F19.opExtrude","CAP_FACE",FACE,{"disambiguationData":[OSD([sQuery(id+"F18.wireOp",EDGE,"E33"),sQuery(id+"F18.wireOp",EDGE,"E34"),sQuery(id+"F18.wireOp",EDGE,"E35"),sQuery(id+"F18.wireOp",EDGE,"E36"),sQuery(id+"F18.wireOp",EDGE,"E37"),sQuery(id+"F18.wireOp",EDGE,"E38"),sQuery(id+"F18.wireOp",EDGE,"E45.filletArc"),sQuery(id+"F18.wireOp",EDGE,"E46.filletArc"),sQuery(id+"F18.wireOp",EDGE,"E47.filletArc"),sQuery(id+"F18.wireOp",EDGE,"E48.filletArc"),sQuery(id+"F18.wireOp",EDGE,"E53"),sQuery(id+"F18.wireOp",EDGE,"E54"),sQuery(id+"F18.wireOp",EDGE,"E55"),sQuery(id+"F18.wireOp",EDGE,"E56"),sQuery(id+"F18.wireOp",EDGE,"E57"),sQuery(id+"F18.wireOp",EDGE,"E58"),sQuery(id+"F18.wireOp",EDGE,"E59"),sQuery(id+"F18.wireOp",EDGE,"E60"),sQuery(id+"F18.wireOp",EDGE,"E61"),sQuery(id+"F18.wireOp",EDGE,"E62"),sQuery(id+"F18.wireOp",EDGE,"E63"),sQuery(id+"F18.wireOp",EDGE,"E64"),sQuery(id+"F18.wireOp",EDGE,"E65.trimOffspring"),sQuery(id+"F18.wireOp",EDGE,"E66.trimOffspring"),sQuery(id+"F18.wireOp",EDGE,"E67.trimOffspring"),sQuery(id+"F18.wireOp",EDGE,"E68.trimOffspring")])],"isStart":false}),makeQuery(id+"F20.opExtrude","SWEPT_FACE",FACE,{"disambiguationData":[OSD([sQuery(id+"F18.wireOp",EDGE,"E39.top")])]})]});
            var Q7;
            Q7=makeQuery(id+"F20.boolean.opBoolean","INTERSECT",EDGE,{"derivedFrom":[makeQuery(id+"F19.opExtrude","CAP_FACE",FACE,{"disambiguationData":[OSD([sQuery(id+"F18.wireOp",EDGE,"E33"),sQuery(id+"F18.wireOp",EDGE,"E34"),sQuery(id+"F18.wireOp",EDGE,"E35"),sQuery(id+"F18.wireOp",EDGE,"E36"),sQuery(id+"F18.wireOp",EDGE,"E37"),sQuery(id+"F18.wireOp",EDGE,"E38"),sQuery(id+"F18.wireOp",EDGE,"E45.filletArc"),sQuery(id+"F18.wireOp",EDGE,"E46.filletArc"),sQuery(id+"F18.wireOp",EDGE,"E47.filletArc"),sQuery(id+"F18.wireOp",EDGE,"E48.filletArc"),sQuery(id+"F18.wireOp",EDGE,"E53"),sQuery(id+"F18.wireOp",EDGE,"E54"),sQuery(id+"F18.wireOp",EDGE,"E55"),sQuery(id+"F18.wireOp",EDGE,"E56"),sQuery(id+"F18.wireOp",EDGE,"E57"),sQuery(id+"F18.wireOp",EDGE,"E58"),sQuery(id+"F18.wireOp",EDGE,"E59"),sQuery(id+"F18.wireOp",EDGE,"E60"),sQuery(id+"F18.wireOp",EDGE,"E61"),sQuery(id+"F18.wireOp",EDGE,"E62"),sQuery(id+"F18.wireOp",EDGE,"E63"),sQuery(id+"F18.wireOp",EDGE,"E64"),sQuery(id+"F18.wireOp",EDGE,"E65.trimOffspring"),sQuery(id+"F18.wireOp",EDGE,"E66.trimOffspring"),sQuery(id+"F18.wireOp",EDGE,"E67.trimOffspring"),sQuery(id+"F18.wireOp",EDGE,"E68.trimOffspring")])],"isStart":false}),makeQuery(id+"F20.opExtrude","SWEPT_FACE",FACE,{"disambiguationData":[OSD([sQuery(id+"F18.wireOp",EDGE,"E39.right")])]})]});
            var Q8;
            Q8=makeQuery(id+"F20.boolean.opBoolean","INTERSECT",EDGE,{"derivedFrom":[makeQuery(id+"F19.opExtrude","CAP_FACE",FACE,{"disambiguationData":[OSD([sQuery(id+"F18.wireOp",EDGE,"E33"),sQuery(id+"F18.wireOp",EDGE,"E34"),sQuery(id+"F18.wireOp",EDGE,"E35"),sQuery(id+"F18.wireOp",EDGE,"E36"),sQuery(id+"F18.wireOp",EDGE,"E37"),sQuery(id+"F18.wireOp",EDGE,"E38"),sQuery(id+"F18.wireOp",EDGE,"E45.filletArc"),sQuery(id+"F18.wireOp",EDGE,"E46.filletArc"),sQuery(id+"F18.wireOp",EDGE,"E47.filletArc"),sQuery(id+"F18.wireOp",EDGE,"E48.filletArc"),sQuery(id+"F18.wireOp",EDGE,"E53"),sQuery(id+"F18.wireOp",EDGE,"E54"),sQuery(id+"F18.wireOp",EDGE,"E55"),sQuery(id+"F18.wireOp",EDGE,"E56"),sQuery(id+"F18.wireOp",EDGE,"E57"),sQuery(id+"F18.wireOp",EDGE,"E58"),sQuery(id+"F18.wireOp",EDGE,"E59"),sQuery(id+"F18.wireOp",EDGE,"E60"),sQuery(id+"F18.wireOp",EDGE,"E61"),sQuery(id+"F18.wireOp",EDGE,"E62"),sQuery(id+"F18.wireOp",EDGE,"E63"),sQuery(id+"F18.wireOp",EDGE,"E64"),sQuery(id+"F18.wireOp",EDGE,"E65.trimOffspring"),sQuery(id+"F18.wireOp",EDGE,"E66.trimOffspring"),sQuery(id+"F18.wireOp",EDGE,"E67.trimOffspring"),sQuery(id+"F18.wireOp",EDGE,"E68.trimOffspring")])],"isStart":false}),makeQuery(id+"F20.opExtrude","SWEPT_FACE",FACE,{"disambiguationData":[OSD([sQuery(id+"F18.wireOp",EDGE,"E51")])]})]});
            var Q9;
            Q9=makeQuery(id+"F20.boolean.opBoolean","INTERSECT",EDGE,{"derivedFrom":[makeQuery(id+"F19.opExtrude","CAP_FACE",FACE,{"disambiguationData":[OSD([sQuery(id+"F18.wireOp",EDGE,"E33"),sQuery(id+"F18.wireOp",EDGE,"E34"),sQuery(id+"F18.wireOp",EDGE,"E35"),sQuery(id+"F18.wireOp",EDGE,"E36"),sQuery(id+"F18.wireOp",EDGE,"E37"),sQuery(id+"F18.wireOp",EDGE,"E38"),sQuery(id+"F18.wireOp",EDGE,"E45.filletArc"),sQuery(id+"F18.wireOp",EDGE,"E46.filletArc"),sQuery(id+"F18.wireOp",EDGE,"E47.filletArc"),sQuery(id+"F18.wireOp",EDGE,"E48.filletArc"),sQuery(id+"F18.wireOp",EDGE,"E53"),sQuery(id+"F18.wireOp",EDGE,"E54"),sQuery(id+"F18.wireOp",EDGE,"E55"),sQuery(id+"F18.wireOp",EDGE,"E56"),sQuery(id+"F18.wireOp",EDGE,"E57"),sQuery(id+"F18.wireOp",EDGE,"E58"),sQuery(id+"F18.wireOp",EDGE,"E59"),sQuery(id+"F18.wireOp",EDGE,"E60"),sQuery(id+"F18.wireOp",EDGE,"E61"),sQuery(id+"F18.wireOp",EDGE,"E62"),sQuery(id+"F18.wireOp",EDGE,"E63"),sQuery(id+"F18.wireOp",EDGE,"E64"),sQuery(id+"F18.wireOp",EDGE,"E65.trimOffspring"),sQuery(id+"F18.wireOp",EDGE,"E66.trimOffspring"),sQuery(id+"F18.wireOp",EDGE,"E67.trimOffspring"),sQuery(id+"F18.wireOp",EDGE,"E68.trimOffspring")])],"isStart":false}),makeQuery(id+"F20.opExtrude","SWEPT_FACE",FACE,{"disambiguationData":[OSD([sQuery(id+"F18.wireOp",EDGE,"E40.top")])]})]});
            var Q10;
            Q10=makeQuery(id+"F20.boolean.opBoolean","INTERSECT",EDGE,{"derivedFrom":[makeQuery(id+"F19.opExtrude","CAP_FACE",FACE,{"disambiguationData":[OSD([sQuery(id+"F18.wireOp",EDGE,"E33"),sQuery(id+"F18.wireOp",EDGE,"E34"),sQuery(id+"F18.wireOp",EDGE,"E35"),sQuery(id+"F18.wireOp",EDGE,"E36"),sQuery(id+"F18.wireOp",EDGE,"E37"),sQuery(id+"F18.wireOp",EDGE,"E38"),sQuery(id+"F18.wireOp",EDGE,"E45.filletArc"),sQuery(id+"F18.wireOp",EDGE,"E46.filletArc"),sQuery(id+"F18.wireOp",EDGE,"E47.filletArc"),sQuery(id+"F18.wireOp",EDGE,"E48.filletArc"),sQuery(id+"F18.wireOp",EDGE,"E53"),sQuery(id+"F18.wireOp",EDGE,"E54"),sQuery(id+"F18.wireOp",EDGE,"E55"),sQuery(id+"F18.wireOp",EDGE,"E56"),sQuery(id+"F18.wireOp",EDGE,"E57"),sQuery(id+"F18.wireOp",EDGE,"E58"),sQuery(id+"F18.wireOp",EDGE,"E59"),sQuery(id+"F18.wireOp",EDGE,"E60"),sQuery(id+"F18.wireOp",EDGE,"E61"),sQuery(id+"F18.wireOp",EDGE,"E62"),sQuery(id+"F18.wireOp",EDGE,"E63"),sQuery(id+"F18.wireOp",EDGE,"E64"),sQuery(id+"F18.wireOp",EDGE,"E65.trimOffspring"),sQuery(id+"F18.wireOp",EDGE,"E66.trimOffspring"),sQuery(id+"F18.wireOp",EDGE,"E67.trimOffspring"),sQuery(id+"F18.wireOp",EDGE,"E68.trimOffspring")])],"isStart":false}),makeQuery(id+"F20.opExtrude","SWEPT_FACE",FACE,{"disambiguationData":[OSD([sQuery(id+"F18.wireOp",EDGE,"E40.left")])]})]});
            var Q11;
            Q11=makeQuery(id+"F20.boolean.opBoolean","INTERSECT",EDGE,{"derivedFrom":[makeQuery(id+"F19.opExtrude","CAP_FACE",FACE,{"disambiguationData":[OSD([sQuery(id+"F18.wireOp",EDGE,"E33"),sQuery(id+"F18.wireOp",EDGE,"E34"),sQuery(id+"F18.wireOp",EDGE,"E35"),sQuery(id+"F18.wireOp",EDGE,"E36"),sQuery(id+"F18.wireOp",EDGE,"E37"),sQuery(id+"F18.wireOp",EDGE,"E38"),sQuery(id+"F18.wireOp",EDGE,"E45.filletArc"),sQuery(id+"F18.wireOp",EDGE,"E46.filletArc"),sQuery(id+"F18.wireOp",EDGE,"E47.filletArc"),sQuery(id+"F18.wireOp",EDGE,"E48.filletArc"),sQuery(id+"F18.wireOp",EDGE,"E53"),sQuery(id+"F18.wireOp",EDGE,"E54"),sQuery(id+"F18.wireOp",EDGE,"E55"),sQuery(id+"F18.wireOp",EDGE,"E56"),sQuery(id+"F18.wireOp",EDGE,"E57"),sQuery(id+"F18.wireOp",EDGE,"E58"),sQuery(id+"F18.wireOp",EDGE,"E59"),sQuery(id+"F18.wireOp",EDGE,"E60"),sQuery(id+"F18.wireOp",EDGE,"E61"),sQuery(id+"F18.wireOp",EDGE,"E62"),sQuery(id+"F18.wireOp",EDGE,"E63"),sQuery(id+"F18.wireOp",EDGE,"E64"),sQuery(id+"F18.wireOp",EDGE,"E65.trimOffspring"),sQuery(id+"F18.wireOp",EDGE,"E66.trimOffspring"),sQuery(id+"F18.wireOp",EDGE,"E67.trimOffspring"),sQuery(id+"F18.wireOp",EDGE,"E68.trimOffspring")])],"isStart":false}),makeQuery(id+"F20.opExtrude","SWEPT_FACE",FACE,{"disambiguationData":[OSD([sQuery(id+"F18.wireOp",EDGE,"E52")])]})]});
            var Q12;
            Q12=makeQuery(id+"F20.boolean.opBoolean","INTERSECT",EDGE,{"derivedFrom":[makeQuery(id+"F19.opExtrude","CAP_FACE",FACE,{"disambiguationData":[OSD([sQuery(id+"F18.wireOp",EDGE,"E33"),sQuery(id+"F18.wireOp",EDGE,"E34"),sQuery(id+"F18.wireOp",EDGE,"E35"),sQuery(id+"F18.wireOp",EDGE,"E36"),sQuery(id+"F18.wireOp",EDGE,"E37"),sQuery(id+"F18.wireOp",EDGE,"E38"),sQuery(id+"F18.wireOp",EDGE,"E45.filletArc"),sQuery(id+"F18.wireOp",EDGE,"E46.filletArc"),sQuery(id+"F18.wireOp",EDGE,"E47.filletArc"),sQuery(id+"F18.wireOp",EDGE,"E48.filletArc"),sQuery(id+"F18.wireOp",EDGE,"E53"),sQuery(id+"F18.wireOp",EDGE,"E54"),sQuery(id+"F18.wireOp",EDGE,"E55"),sQuery(id+"F18.wireOp",EDGE,"E56"),sQuery(id+"F18.wireOp",EDGE,"E57"),sQuery(id+"F18.wireOp",EDGE,"E58"),sQuery(id+"F18.wireOp",EDGE,"E59"),sQuery(id+"F18.wireOp",EDGE,"E60"),sQuery(id+"F18.wireOp",EDGE,"E61"),sQuery(id+"F18.wireOp",EDGE,"E62"),sQuery(id+"F18.wireOp",EDGE,"E63"),sQuery(id+"F18.wireOp",EDGE,"E64"),sQuery(id+"F18.wireOp",EDGE,"E65.trimOffspring"),sQuery(id+"F18.wireOp",EDGE,"E66.trimOffspring"),sQuery(id+"F18.wireOp",EDGE,"E67.trimOffspring"),sQuery(id+"F18.wireOp",EDGE,"E68.trimOffspring")])],"isStart":false}),makeQuery(id+"F20.opExtrude","SWEPT_FACE",FACE,{"disambiguationData":[OSD([sQuery(id+"F18.wireOp",EDGE,"E40.right")])]})]});
            var Q13;
            Q13=makeQuery(id+"F20.boolean.opBoolean","INTERSECT",EDGE,{"derivedFrom":[makeQuery(id+"F19.opExtrude","CAP_FACE",FACE,{"disambiguationData":[OSD([sQuery(id+"F18.wireOp",EDGE,"E33"),sQuery(id+"F18.wireOp",EDGE,"E34"),sQuery(id+"F18.wireOp",EDGE,"E35"),sQuery(id+"F18.wireOp",EDGE,"E36"),sQuery(id+"F18.wireOp",EDGE,"E37"),sQuery(id+"F18.wireOp",EDGE,"E38"),sQuery(id+"F18.wireOp",EDGE,"E45.filletArc"),sQuery(id+"F18.wireOp",EDGE,"E46.filletArc"),sQuery(id+"F18.wireOp",EDGE,"E47.filletArc"),sQuery(id+"F18.wireOp",EDGE,"E48.filletArc"),sQuery(id+"F18.wireOp",EDGE,"E53"),sQuery(id+"F18.wireOp",EDGE,"E54"),sQuery(id+"F18.wireOp",EDGE,"E55"),sQuery(id+"F18.wireOp",EDGE,"E56"),sQuery(id+"F18.wireOp",EDGE,"E57"),sQuery(id+"F18.wireOp",EDGE,"E58"),sQuery(id+"F18.wireOp",EDGE,"E59"),sQuery(id+"F18.wireOp",EDGE,"E60"),sQuery(id+"F18.wireOp",EDGE,"E61"),sQuery(id+"F18.wireOp",EDGE,"E62"),sQuery(id+"F18.wireOp",EDGE,"E63"),sQuery(id+"F18.wireOp",EDGE,"E64"),sQuery(id+"F18.wireOp",EDGE,"E65.trimOffspring"),sQuery(id+"F18.wireOp",EDGE,"E66.trimOffspring"),sQuery(id+"F18.wireOp",EDGE,"E67.trimOffspring"),sQuery(id+"F18.wireOp",EDGE,"E68.trimOffspring")])],"isStart":false}),makeQuery(id+"F20.opExtrude","SWEPT_FACE",FACE,{"disambiguationData":[OSD([sQuery(id+"F18.wireOp",EDGE,"E40.bottom")])]})]});
            fillet(context, id + "F21", {"entities" : qUnion([Q0, Q1, Q2, Q3, Q4, Q5, Q6, Q7, Q8, Q9, Q10, Q11, Q12, Q13]), "tangentPropagation" : true, "radius" : 1 * mm, "defaultsChanged" : true, "vertexSettings" : [], "allowEdgeOverflow" : false});
        }
    });
